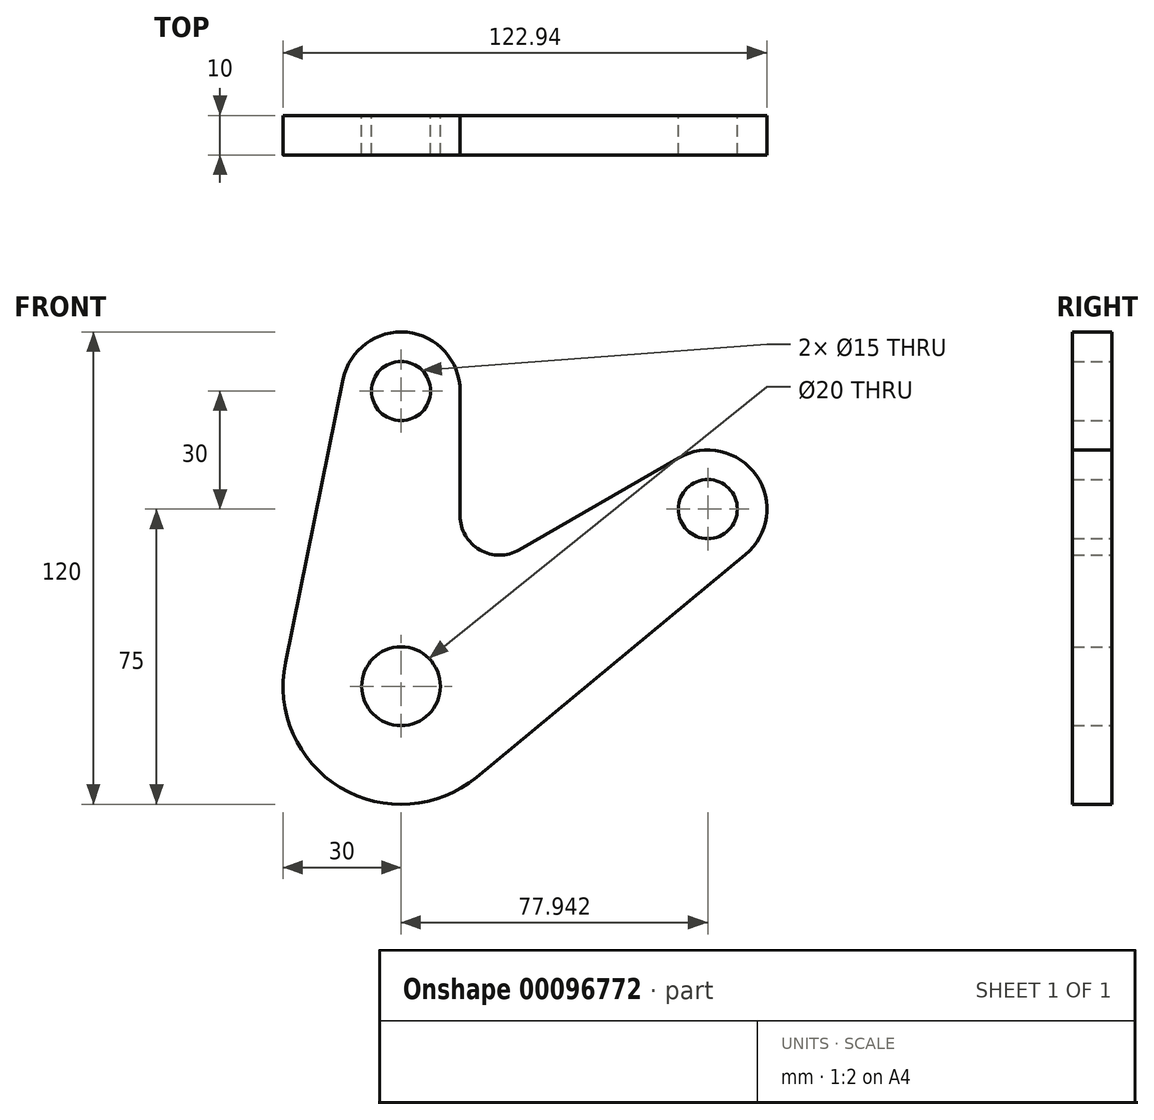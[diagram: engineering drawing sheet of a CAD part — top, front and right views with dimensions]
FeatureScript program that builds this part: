
annotation { "Feature Type Name" : "Feature", "Feature Type Description" : "" }
export const myFeature = defineFeature(function(context is Context, id is Id, definition is map)
    precondition{}
    {
        {
            var Q0;
            Q0=qCreatedBy(makeId("Front.planeOp"),FACE);
            var sketch = newSketch(context, id + "F0", { "sketchPlane" : qUnion([Q0])});
            skLineSegment(sketch, "E0", {"start": v(0, 0) * mm, "end": v(0, 75) * mm, "construction": true});
            skLineSegment(sketch, "E1", {"start": v(0, 0) * mm, "end": v(77.94, 45) * mm, "construction": true});
            skCircle(sketch, "E2", {"center": v(0, 75) * mm, "radius": 7.5 * mm});
            skCircle(sketch, "E3", {"center": v(0, 0) * mm, "radius": 10 * mm});
            skCircle(sketch, "E4", {"center": v(77.94, 45) * mm, "radius": 7.5 * mm});
            skLineSegment(sketch, "E5", {"start": v(15, 75) * mm, "end": v(15, 43.3) * mm});
            skLineSegment(sketch, "E6", {"start": v(30, 34.64) * mm, "end": v(70.44, 58) * mm});
            skArc(sketch, "E7", {"start": v(15, 43.3) * mm, "mid": v(20, 34.64) * mm, "end": v(30, 34.64) * mm});
            skLineSegment(sketch, "E8", {"start": v(19.12, -23.12) * mm, "end": v(87.5, 33.44) * mm});
            skArc(sketch, "E9", {"start": v(70.44, 58) * mm, "mid": v(90.26, 53.56) * mm, "end": v(87.5, 33.44) * mm});
            skArc(sketch, "E10", {"start": v(-14.7, 78) * mm, "mid": v(1.5, 89.92) * mm, "end": v(15, 75) * mm});
            skArc(sketch, "E11", {"start": v(-29.4, 6) * mm, "mid": v(-15.44, -25.72) * mm, "end": v(19.12, -23.12) * mm});
            skLineSegment(sketch, "E12", {"start": v(-14.7, 78) * mm, "end": v(-29.4, 6) * mm});
            skSolve(sketch);
        }
        {
            var Q0;
            Q0 = qSketchRegion(id + "F0", true);
            extrude(context, id + "F1", {"entities" : qUnion([Q0]), "depth" : 10 * mm});
        }
    });
